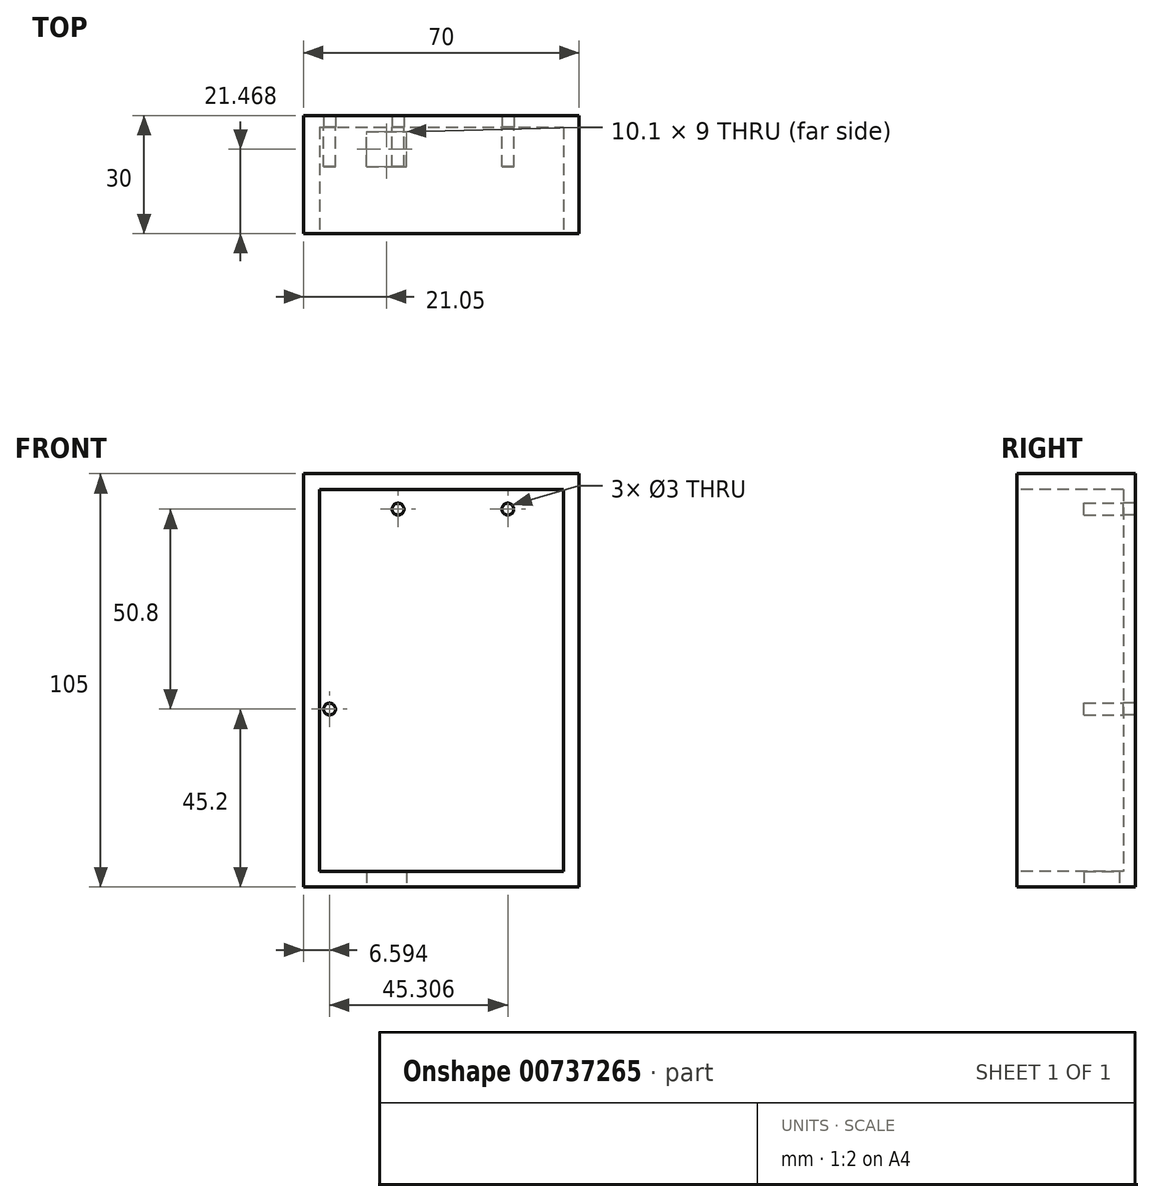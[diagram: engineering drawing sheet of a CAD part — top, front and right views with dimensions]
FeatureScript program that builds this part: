
annotation { "Feature Type Name" : "Feature", "Feature Type Description" : "" }
export const myFeature = defineFeature(function(context is Context, id is Id, definition is map)
    precondition{}
    {
        {
            var Q0;
            Q0=qCreatedBy(makeId("Front.planeOp"),FACE);
            var sketch = newSketch(context, id + "F0", { "sketchPlane" : qUnion([Q0])});
            skLineSegment(sketch, "E0.bottom", {"start": v(0, 0) * mm, "end": v(70, 0) * mm});
            skLineSegment(sketch, "E0.top", {"start": v(0, 105) * mm, "end": v(70, 105) * mm});
            skLineSegment(sketch, "E0.left", {"start": v(0, 0) * mm, "end": v(0, 105) * mm});
            skLineSegment(sketch, "E0.right", {"start": v(70, 0) * mm, "end": v(70, 105) * mm});
            skSolve(sketch);
        }
        {
            var Q0;
            Q0 = qSketchRegion(id + "F0", true);
            extrude(context, id + "F1", {"entities" : qUnion([Q0]), "depth" : 30 * mm, "offsetDistance" : 25 * mm});
        }
        {
            var Q0;
            Q0=makeQuery(id+"F1.opExtrude","CAP_FACE",FACE,{"disambiguationData":[OSD([sQuery(id+"F0.wireOp",EDGE,"E0.bottom"),sQuery(id+"F0.wireOp",EDGE,"E0.top"),sQuery(id+"F0.wireOp",EDGE,"E0.left"),sQuery(id+"F0.wireOp",EDGE,"E0.right")])],"isStart":false});
            var sketch = newSketch(context, id + "F2", { "sketchPlane" : qUnion([Q0])});
            skLineSegment(sketch, "E1.bottom", {"start": v(4, 101) * mm, "end": v(66, 101) * mm});
            skLineSegment(sketch, "E1.top", {"start": v(4, 4) * mm, "end": v(66, 4) * mm});
            skLineSegment(sketch, "E1.left", {"start": v(4, 101) * mm, "end": v(4, 4) * mm});
            skLineSegment(sketch, "E1.right", {"start": v(66, 101) * mm, "end": v(66, 4) * mm});
            skSolve(sketch);
        }
        {
            var Q0;
            Q0 = qSketchRegion(id + "F2", true);
            extrude(context, id + "F3", {"entities" : qUnion([Q0]), "operationType" : NewBodyOperationType.REMOVE, "oppositeDirection" : true, "depth" : 27 * mm, "offsetDistance" : 25 * mm});
        }
        {
            var Q0;
            Q0=makeQuery(id+"F3.boolean.opBoolean","COPY",FACE,{"derivedFrom":makeQuery(id+"F3.opExtrude","CAP_FACE",FACE,{"disambiguationData":[OSD([sQuery(id+"F2.wireOp",EDGE,"E1.bottom"),sQuery(id+"F2.wireOp",EDGE,"E1.top"),sQuery(id+"F2.wireOp",EDGE,"E1.left"),sQuery(id+"F2.wireOp",EDGE,"E1.right")])],"isStart":false})});
            var sketch = newSketch(context, id + "F4", { "sketchPlane" : qUnion([Q0])});
            skCircle(sketch, "E2", {"center": v(24, 96) * mm, "radius": 1.5 * mm});
            skCircle(sketch, "E3", {"center": v(51.9, 96) * mm, "radius": 1.5 * mm});
            skCircle(sketch, "E4", {"center": v(6.6, 45.2) * mm, "radius": 1.5 * mm});
            skSolve(sketch);
        }
        {
            var Q0;
            Q0 = qSketchRegion(id + "F4", true);
            extrude(context, id + "F5", {"entities" : qUnion([Q0]), "operationType" : NewBodyOperationType.REMOVE, "oppositeDirection" : true, "depth" : 25 * mm, "offsetDistance" : 25 * mm});
        }
        {
            var Q0;
            Q0 = qSketchRegion(id + "F4", true);
            extrude(context, id + "F6", {"entities" : qUnion([Q0]), "depth" : 10 * mm, "offsetDistance" : 25 * mm});
        }
        {
            var Q0;
            Q0=makeQuery(id+"F1.opExtrude","SWEPT_FACE",FACE,{"disambiguationData":[OSD([sQuery(id+"F0.wireOp",EDGE,"E0.bottom")])]});
            var sketch = newSketch(context, id + "F7", { "sketchPlane" : qUnion([Q0])});
            skLineSegment(sketch, "E5.bottom", {"start": v(16, 13.03) * mm, "end": v(26.1, 13.03) * mm});
            skLineSegment(sketch, "E5.top", {"start": v(16, 4.03) * mm, "end": v(26.1, 4.03) * mm});
            skLineSegment(sketch, "E5.left", {"start": v(16, 13.03) * mm, "end": v(16, 4.03) * mm});
            skLineSegment(sketch, "E5.right", {"start": v(26.1, 13.03) * mm, "end": v(26.1, 4.03) * mm});
            skSolve(sketch);
        }
        {
            var Q0;
            Q0 = qSketchRegion(id + "F7", true);
            extrude(context, id + "F8", {"entities" : qUnion([Q0]), "operationType" : NewBodyOperationType.REMOVE, "oppositeDirection" : true, "depth" : 25 * mm, "offsetDistance" : 25 * mm});
        }
        {
            var Q0;
            Q0 = qSketchRegion(id + "F7", true);
            extrude(context, id + "F9", {"entities" : qUnion([Q0]), "operationType" : NewBodyOperationType.REMOVE, "oppositeDirection" : true, "depth" : 25 * mm, "offsetDistance" : 25 * mm});
        }
    });
